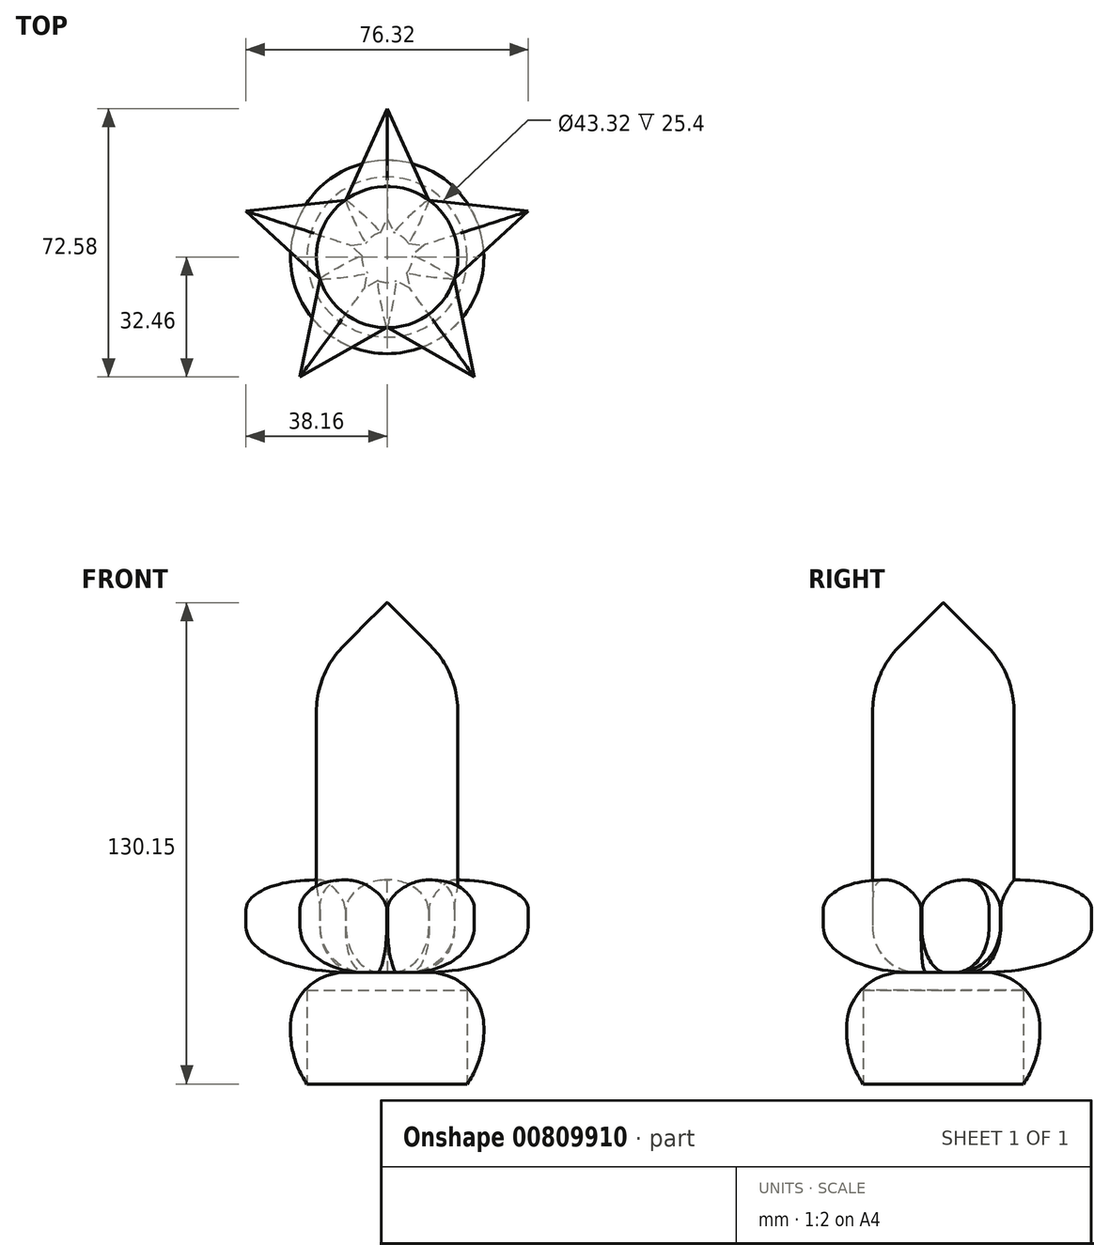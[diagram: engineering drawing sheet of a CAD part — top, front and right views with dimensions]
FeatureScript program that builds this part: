
annotation { "Feature Type Name" : "Feature", "Feature Type Description" : "" }
export const myFeature = defineFeature(function(context is Context, id is Id, definition is map)
    precondition{}
    {
        {
            var Q0;
            Q0=qCreatedBy(makeId("Top.planeOp"),FACE);
            var sketch = newSketch(context, id + "F0", { "sketchPlane" : qUnion([Q0])});
            skCircle(sketch, "E0", {"center": v(0, 0) * mm, "radius": 19.11 * mm});
            skLineSegment(sketch, "E1", {"start": v(-11.15, 15.53) * mm, "end": v(0, 40.12) * mm});
            skLineSegment(sketch, "E2", {"start": v(0, 40.12) * mm, "end": v(11.15, 15.53) * mm});
            skLineSegment(sketch, "E3.1.0", {"start": v(-38.16, 12.4) * mm, "end": v(-11.32, 15.4) * mm});
            skLineSegment(sketch, "E3.1.1", {"start": v(-18.21, -5.8) * mm, "end": v(-38.16, 12.4) * mm});
            skLineSegment(sketch, "E3.2.0", {"start": v(-23.58, -32.46) * mm, "end": v(-18.14, -6) * mm});
            skLineSegment(sketch, "E3.2.1", {"start": v(-0.1, -19.11) * mm, "end": v(-23.58, -32.46) * mm});
            skLineSegment(sketch, "E3.3.0", {"start": v(23.58, -32.46) * mm, "end": v(0.1, -19.11) * mm});
            skLineSegment(sketch, "E3.3.1", {"start": v(18.14, -6) * mm, "end": v(23.58, -32.46) * mm});
            skLineSegment(sketch, "E3.4.0", {"start": v(38.16, 12.4) * mm, "end": v(18.21, -5.8) * mm});
            skLineSegment(sketch, "E3.4.1", {"start": v(11.32, 15.4) * mm, "end": v(38.16, 12.4) * mm});
            skSolve(sketch);
        }
        {
            var Q0;
            Q0=makeQuery(id+"F0.imprint","IMPRINT",FACE,{"disambiguationData":[TD([[makeQuery(id+"F0.imprint","IMPRINT",EDGE,{"derivedFrom":sQuery(id+"F0.wireOp",EDGE,"E0")}),1.0]])]});
            extrude(context, id + "F1", {"entities" : qUnion([Q0]), "depth" : 100 * mm, "offsetDistance" : 25.4 * mm});
        }
        {
            var Q0;
            Q0=makeQuery(id+"F1.opExtrude","CAP_EDGE",EDGE,{"disambiguationData":[OSD([sQuery(id+"F0.wireOp",EDGE,"E0")])],"isStart":false});
            chamfer(context, id + "F2", {"entities" : qUnion([Q0]), "width" : 19 * mm, "tangentPropagation" : true});
        }
        {
            var Q0;
            {var subQ0=sQuery(id+"F0.wireOp",EDGE,"E3.1.0");Q0=makeQuery(id+"F0.imprint","IMPRINT",FACE,{"disambiguationData":[TD([[makeQuery(id+"F0.imprint","IMPRINT",EDGE,{"derivedFrom":subQ0}),-1.0]])]});}
            var Q1;
            {var subQ0=sQuery(id+"F0.wireOp",EDGE,"E1");Q1=makeQuery(id+"F0.imprint","IMPRINT",FACE,{"disambiguationData":[TD([[makeQuery(id+"F0.imprint","IMPRINT",EDGE,{"derivedFrom":subQ0}),-1.0]])]});}
            var Q2;
            {var subQ0=sQuery(id+"F0.wireOp",EDGE,"E3.4.0");Q2=makeQuery(id+"F0.imprint","IMPRINT",FACE,{"disambiguationData":[TD([[makeQuery(id+"F0.imprint","IMPRINT",EDGE,{"derivedFrom":subQ0}),-1.0]])]});}
            var Q3;
            {var subQ0=sQuery(id+"F0.wireOp",EDGE,"E3.2.0");Q3=makeQuery(id+"F0.imprint","IMPRINT",FACE,{"disambiguationData":[TD([[makeQuery(id+"F0.imprint","IMPRINT",EDGE,{"derivedFrom":subQ0}),-1.0]])]});}
            var Q4;
            {var subQ0=sQuery(id+"F0.wireOp",EDGE,"E3.3.0");Q4=makeQuery(id+"F0.imprint","IMPRINT",FACE,{"disambiguationData":[TD([[makeQuery(id+"F0.imprint","IMPRINT",EDGE,{"derivedFrom":subQ0}),-1.0]])]});}
            extrude(context, id + "F3", {"entities" : qUnion([Q0, Q1, Q2, Q3, Q4]), "operationType" : NewBodyOperationType.ADD, "depth" : 25 * mm, "offsetDistance" : 25.4 * mm});
        }
        {
            var Q0;
            {var subQ0=sQuery(id+"F0.wireOp",EDGE,"E0");Q0=makeQuery(id+"F3.boolean.opBoolean","MERGE",FACE,{"derivedFrom":[makeQuery(id+"F1.opExtrude","CAP_FACE",FACE,{"disambiguationData":[OSD([subQ0])],"isStart":true}),makeQuery(id+"F3.opExtrude","CAP_FACE",FACE,{"disambiguationData":[OSD([subQ0,sQuery(id+"F0.wireOp",EDGE,"E1"),sQuery(id+"F0.wireOp",EDGE,"E2")])],"isStart":true}),makeQuery(id+"F3.opExtrude","CAP_FACE",FACE,{"disambiguationData":[OSD([subQ0,sQuery(id+"F0.wireOp",EDGE,"E3.1.0"),sQuery(id+"F0.wireOp",EDGE,"E3.1.1")])],"isStart":true}),makeQuery(id+"F3.opExtrude","CAP_FACE",FACE,{"disambiguationData":[OSD([subQ0,sQuery(id+"F0.wireOp",EDGE,"E3.2.0"),sQuery(id+"F0.wireOp",EDGE,"E3.2.1")])],"isStart":true}),makeQuery(id+"F3.opExtrude","CAP_FACE",FACE,{"disambiguationData":[OSD([subQ0,sQuery(id+"F0.wireOp",EDGE,"E3.3.0"),sQuery(id+"F0.wireOp",EDGE,"E3.3.1")])],"isStart":true}),makeQuery(id+"F3.opExtrude","CAP_FACE",FACE,{"disambiguationData":[OSD([subQ0,sQuery(id+"F0.wireOp",EDGE,"E3.4.0"),sQuery(id+"F0.wireOp",EDGE,"E3.4.1")])],"isStart":true})]});}
            fillet(context, id + "F4", {"entities" : qUnion([Q0]), "radius" : 12.26 * mm, "tangentPropagation" : true, "allowEdgeOverflow" : false});
        }
        {
            var Q0;
            Q0=qCreatedBy(makeId("Top.planeOp"),FACE);
            var sketch = newSketch(context, id + "F5", { "sketchPlane" : qUnion([Q0])});
            skCircle(sketch, "E4", {"center": v(0, 0) * mm, "radius": 26.14 * mm});
            skSolve(sketch);
        }
        {
            var Q0;
            Q0 = qSketchRegion(id + "F5", true);
            extrude(context, id + "F6", {"entities" : qUnion([Q0]), "operationType" : NewBodyOperationType.ADD, "depth" : -30.15 * mm, "offsetDistance" : 25.4 * mm});
        }
        {
            var Q0;
            Q0=makeQuery(id+"F6.opExtrude","CAP_FACE",FACE,{"disambiguationData":[OSD([sQuery(id+"F5.wireOp",EDGE,"E4")])],"isStart":false});
            var sketch = newSketch(context, id + "F7", { "sketchPlane" : qUnion([Q0])});
            skCircle(sketch, "E5", {"center": v(0, 0) * mm, "radius": 21.66 * mm});
            skCircle(sketch, "E6", {"center": v(-37.1, 0) * mm, "radius": 10.58 * mm});
            skCircle(sketch, "E7.1.0", {"center": v(0, -37.1) * mm, "radius": 10.58 * mm});
            skCircle(sketch, "E7.2.0", {"center": v(37.1, 0) * mm, "radius": 10.58 * mm});
            skCircle(sketch, "E7.3.0", {"center": v(0, 37.1) * mm, "radius": 10.58 * mm});
            skSolve(sketch);
        }
        {
            var Q0;
            Q0 = qSketchRegion(id + "F7", true);
            extrude(context, id + "F8", {"entities" : qUnion([Q0]), "operationType" : NewBodyOperationType.REMOVE, "oppositeDirection" : true, "depth" : 25.4 * mm, "offsetDistance" : 25.4 * mm});
        }
        {
            var Q0;
            Q0=makeQuery(id+"F3.opExtrude","CAP_EDGE",EDGE,{"disambiguationData":[OSD([sQuery(id+"F0.wireOp",EDGE,"E3.2.0")])],"isStart":false});
            var Q1;
            Q1=makeQuery(id+"F3.opExtrude","CAP_EDGE",EDGE,{"disambiguationData":[OSD([sQuery(id+"F0.wireOp",EDGE,"E3.2.1")])],"isStart":false});
            var Q2;
            Q2=makeQuery(id+"F3.opExtrude","CAP_EDGE",EDGE,{"disambiguationData":[OSD([sQuery(id+"F0.wireOp",EDGE,"E3.1.1")])],"isStart":false});
            var Q3;
            Q3=makeQuery(id+"F3.opExtrude","CAP_EDGE",EDGE,{"disambiguationData":[OSD([sQuery(id+"F0.wireOp",EDGE,"E3.1.0")])],"isStart":false});
            var Q4;
            Q4=makeQuery(id+"F3.opExtrude","CAP_EDGE",EDGE,{"disambiguationData":[OSD([sQuery(id+"F0.wireOp",EDGE,"E1")])],"isStart":false});
            var Q5;
            Q5=makeQuery(id+"F3.opExtrude","CAP_EDGE",EDGE,{"disambiguationData":[OSD([sQuery(id+"F0.wireOp",EDGE,"E2")])],"isStart":false});
            var Q6;
            Q6=makeQuery(id+"F3.opExtrude","CAP_EDGE",EDGE,{"disambiguationData":[OSD([sQuery(id+"F0.wireOp",EDGE,"E3.4.1")])],"isStart":false});
            var Q7;
            Q7=makeQuery(id+"F3.opExtrude","CAP_EDGE",EDGE,{"disambiguationData":[OSD([sQuery(id+"F0.wireOp",EDGE,"E3.4.0")])],"isStart":false});
            var Q8;
            Q8=makeQuery(id+"F3.opExtrude","CAP_EDGE",EDGE,{"disambiguationData":[OSD([sQuery(id+"F0.wireOp",EDGE,"E3.3.1")])],"isStart":false});
            var Q9;
            Q9=makeQuery(id+"F3.opExtrude","CAP_EDGE",EDGE,{"disambiguationData":[OSD([sQuery(id+"F0.wireOp",EDGE,"E3.3.0")])],"isStart":false});
            fillet(context, id + "F9", {"entities" : qUnion([Q0, Q1, Q2, Q3, Q4, Q5, Q6, Q7, Q8, Q9]), "radius" : 7.97 * mm, "tangentPropagation" : true, "allowEdgeOverflow" : false});
        }
        {
            var Q0;
            Q0=makeQuery(id+"F6.opExtrude","CAP_EDGE",EDGE,{"disambiguationData":[OSD([sQuery(id+"F5.wireOp",EDGE,"E4")])],"isStart":true});
            fillet(context, id + "F10", {"entities" : qUnion([Q0]), "radius" : 14.8 * mm, "tangentPropagation" : true, "allowEdgeOverflow" : false});
        }
        {
            var Q0;
            Q0=makeQuery(id+"F6.opExtrude","CAP_EDGE",EDGE,{"disambiguationData":[OSD([sQuery(id+"F5.wireOp",EDGE,"E4")])],"isStart":false});
            fillet(context, id + "F11", {"entities" : qUnion([Q0]), "radius" : 25.4 * mm, "tangentPropagation" : true, "allowEdgeOverflow" : false});
        }
        {
            var Q0;
            {var subQ0=sQuery(id+"F0.wireOp",EDGE,"E0");Q0=makeQuery(id+"F2.opChamfer","BLEND_EDGE",EDGE,{"blendedFrom":[makeQuery(id+"F1.opExtrude","CAP_EDGE",EDGE,{"disambiguationData":[OSD([subQ0])],"isStart":false}),makeQuery(id+"F1.opExtrude","SWEPT_FACE",FACE,{"disambiguationData":[OSD([subQ0])]})],"blendedInto":[makeQuery(id+"F1.opExtrude","SWEPT_FACE",FACE,{"disambiguationData":[OSD([subQ0])]})]});}
            fillet(context, id + "F12", {"entities" : qUnion([Q0]), "radius" : 25.4 * mm, "tangentPropagation" : true, "allowEdgeOverflow" : false});
        }
    });
